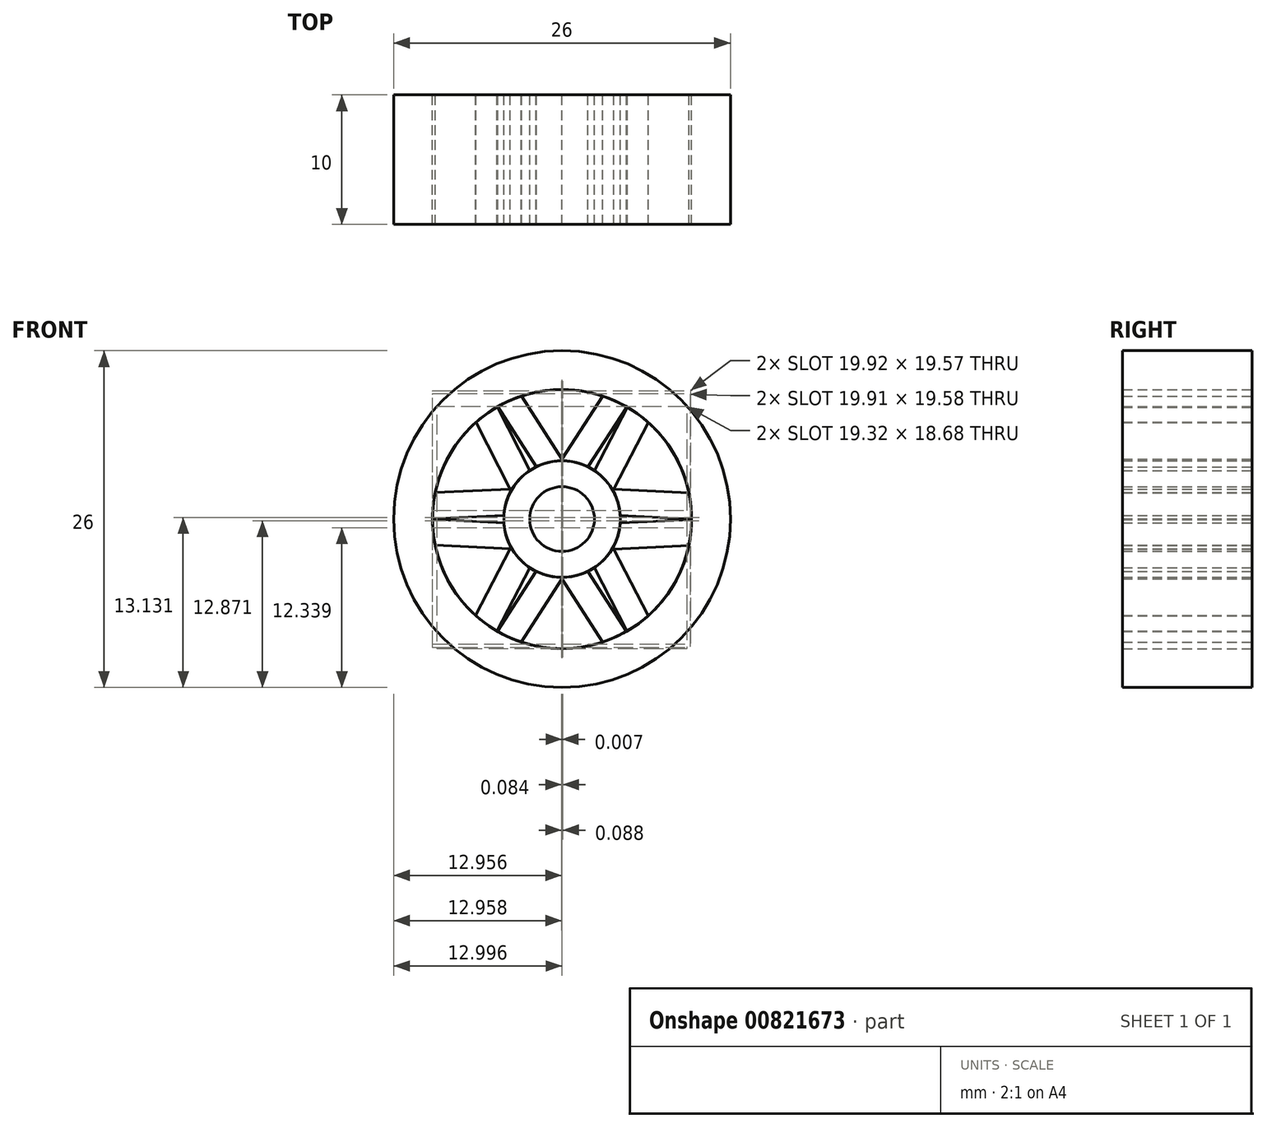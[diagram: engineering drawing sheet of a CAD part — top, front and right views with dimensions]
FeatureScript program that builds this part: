
annotation { "Feature Type Name" : "Feature", "Feature Type Description" : "" }
export const myFeature = defineFeature(function(context is Context, id is Id, definition is map)
    precondition{}
    {
        {
            var Q0;
            Q0=qCreatedBy(makeId("Front.planeOp"),FACE);
            var sketch = newSketch(context, id + "F0", { "sketchPlane" : qUnion([Q0])});
            skCircle(sketch, "E0", {"center": v(0, 0) * mm, "radius": 2.5 * mm});
            skCircle(sketch, "E1", {"center": v(0, 0) * mm, "radius": 13 * mm});
            skLineSegment(sketch, "E2", {"start": v(-3.12, 9.5) * mm, "end": v(0.09, 4.5) * mm});
            skLineSegment(sketch, "E3", {"start": v(-4.97, 8.68) * mm, "end": v(-2, 4.03) * mm});
            skArc(sketch, "E4", {"start": v(-3.12, 9.5) * mm, "mid": v(-4.07, 9.14) * mm, "end": v(-4.97, 8.68) * mm});
            skArc(sketch, "E5", {"start": v(0.09, 4.5) * mm, "mid": v(-0.98, 4.4) * mm, "end": v(-2, 4.03) * mm});
            skCircle(sketch, "E6", {"center": v(0, 0) * mm, "radius": 4.5 * mm});
            skCircle(sketch, "E7", {"center": v(0, 0) * mm, "radius": 10 * mm});
            skLineSegment(sketch, "E8", {"start": v(-93.78, 27.44) * mm, "end": v(-87.12, 27.44) * mm, "construction": true});
            skLineSegment(sketch, "E9", {"start": v(0, 0) * mm, "end": v(0.09, 60.27) * mm, "construction": true});
            skLineSegment(sketch, "E10.MirrorCS", {"start": v(3.15, 9.5) * mm, "end": v(-0.07, 4.5) * mm});
            skLineSegment(sketch, "E11.MirrorCS", {"start": v(5, 8.66) * mm, "end": v(2, 4.03) * mm});
            skSolve(sketch);
        }
        {
            var Q0;
            Q0 = qSketchRegion(id + "F0", true);
            var Q1;
            {var subQ0=sQuery(id+"F0.wireOp",EDGE,"E2");Q1=makeQuery(id+"F0.imprint","IMPRINT",FACE,{"disambiguationData":[TD([[makeQuery(id+"F0.imprint","IMPRINT",EDGE,{"derivedFrom":subQ0}),-1.0]])]});}
            var Q2;
            Q2=makeQuery(id+"F0.imprint","IMPRINT",FACE,{"disambiguationData":[TD([[makeQuery(id+"F0.imprint","IMPRINT",EDGE,{"derivedFrom":sQuery(id+"F0.wireOp",EDGE,"E0")}),-1.0]])]});
            var Q3;
            {var subQ3=sQuery(id+"F0.wireOp",EDGE,"E3");Q3=makeQuery(id+"F0.imprint","IMPRINT",FACE,{"disambiguationData":[TD([[makeQuery(id+"F0.imprint","IMPRINT",EDGE,{"derivedFrom":subQ3}),1.0]])]});}
            var Q4;
            {var subQ3=sQuery(id+"F0.wireOp",EDGE,"E11.MirrorCS");Q4=makeQuery(id+"F0.imprint","IMPRINT",FACE,{"disambiguationData":[TD([[makeQuery(id+"F0.imprint","IMPRINT",EDGE,{"derivedFrom":subQ3}),-1.0]])]});}
            extrude(context, id + "F1", {"entities" : qUnion([Q0, Q1, Q2, Q3, Q4]), "depth" : 5 * mm, "offsetDistance" : 25 * mm});
        }
        {
            var Q0;
            Q0 = qSketchRegion(id + "F0", true);
            var Q1;
            Q1=makeQuery(id+"F1.opExtrude","CAP_FACE",FACE,{"disambiguationData":[OSD([sQuery(id+"F0.wireOp",EDGE,"E0"),sQuery(id+"F0.wireOp",EDGE,"E1"),sQuery(id+"F0.wireOp",EDGE,"E2"),sQuery(id+"F0.wireOp",EDGE,"E3"),sQuery(id+"F0.wireOp",EDGE,"E6"),sQuery(id+"F0.wireOp",EDGE,"E7")])],"isStart":false});
            extrude(context, id + "F2", {"entities" : qUnion([Q0, Q1]), "operationType" : NewBodyOperationType.ADD, "depth" : 5 * mm, "offsetDistance" : 25 * mm});
        }
        {
            var Q0;
            Q0=makeQuery(id+"F1.opExtrude","SWEPT_BODY",BODY,{"disambiguationData":[OSD([sQuery(id+"F0.wireOp",EDGE,"E0"),sQuery(id+"F0.wireOp",EDGE,"E1"),sQuery(id+"F0.wireOp",EDGE,"E2"),sQuery(id+"F0.wireOp",EDGE,"E3"),sQuery(id+"F0.wireOp",EDGE,"E6"),sQuery(id+"F0.wireOp",EDGE,"E7")])]});
            var Q1;
            Q1=makeQuery(id+"F2.opExtrude","CAP_EDGE",EDGE,{"disambiguationData":[OSD([sQuery(id+"F0.wireOp",EDGE,"E0")])],"isStart":false});
            circularPattern(context, id + "F3", {"entities" : qUnion([Q0]), "axis" : qUnion([Q1]), "angle" : 360 * degree, "instanceCount" : 6, "equalSpace" : true});
        }
    });
